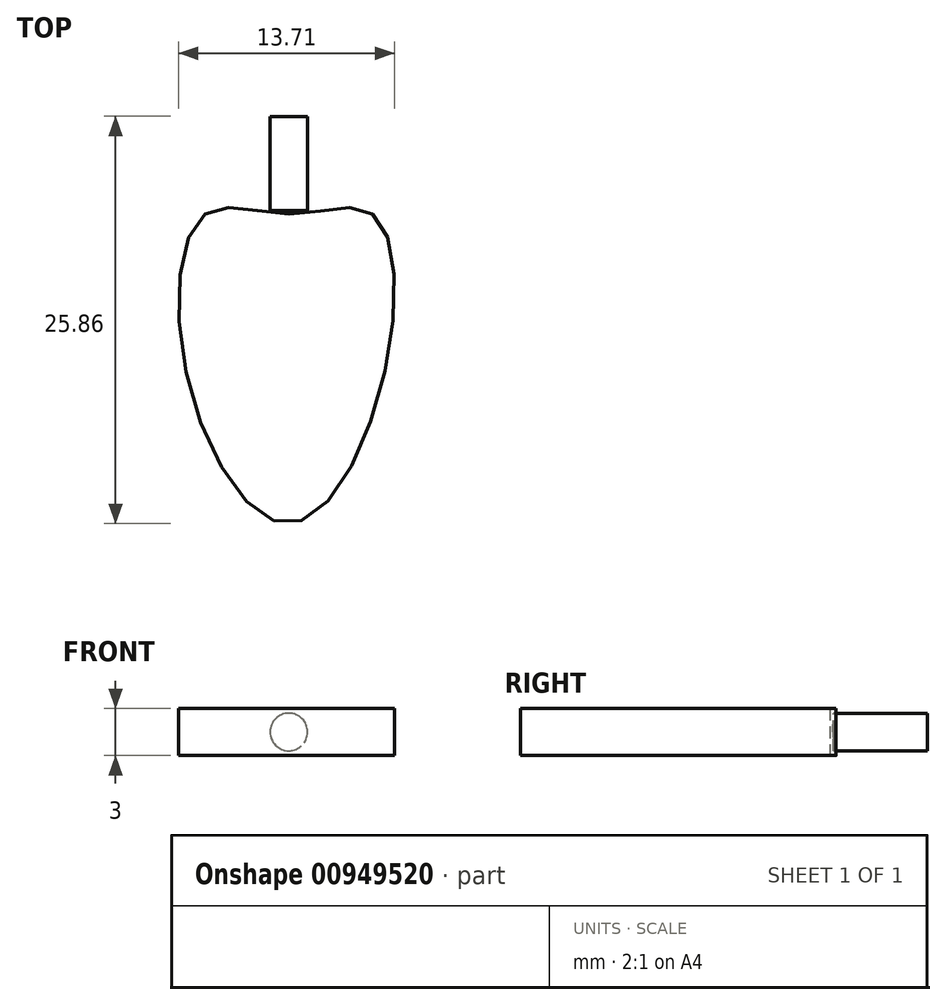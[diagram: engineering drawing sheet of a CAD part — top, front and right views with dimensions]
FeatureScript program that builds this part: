
annotation { "Feature Type Name" : "Feature", "Feature Type Description" : "" }
export const myFeature = defineFeature(function(context is Context, id is Id, definition is map)
    precondition{}
    {
        {
            var Q0;
            Q0=qCreatedBy(makeId("Top.planeOp"),FACE);
            var sketch = newSketch(context, id + "F0", { "sketchPlane" : qUnion([Q0])});
            skFitSpline(sketch, "E0", {"points": [v(0, 8.61) * mm, v(-5.3, 8.61) * mm, v(-6.32, -2.36) * mm, v(0, -11.04) * mm, v(5.93, -2.1) * mm, v(5.3, 8.61) * mm, v(0, 8.61) * mm]});
            skSolve(sketch);
        }
        {
            var Q0;
            Q0=makeQuery(id+"F0.imprint","IMPRINT",FACE,{"disambiguationData":[TD([[makeQuery(id+"F0.imprint","IMPRINT",EDGE,{"derivedFrom":sQuery(id+"F0.wireOp",EDGE,"E0")}),1.0]])]});
            extrude(context, id + "F1", {"entities" : qUnion([Q0]), "endBound" : BoundingType.SYMMETRIC, "depth" : 3 * mm, "offsetDistance" : 25.4 * mm});
        }
        {
            var Q0;
            Q0=qCreatedBy(makeId("Top.planeOp"),FACE);
            var sketch = newSketch(context, id + "F2", { "sketchPlane" : qUnion([Q0])});
            skLineSegment(sketch, "E1", {"start": v(-1.2, 8.85) * mm, "end": v(-1.2, 14.82) * mm});
            skLineSegment(sketch, "E2", {"start": v(0, 8.8) * mm, "end": v(0, 14.82) * mm});
            skLineSegment(sketch, "E3", {"start": v(0, 14.82) * mm, "end": v(-1.2, 14.82) * mm});
            skLineSegment(sketch, "E4", {"start": v(-1.2, 8.85) * mm, "end": v(0, 8.8) * mm});
            skSolve(sketch);
        }
        {
            var Q0;
            Q0=makeQuery(id+"F2.imprint","IMPRINT",FACE,{"disambiguationData":[TD([[makeQuery(id+"F2.imprint","IMPRINT",EDGE,{"derivedFrom":sQuery(id+"F2.wireOp",EDGE,"E1")}),-1.0]])]});
            var Q1;
            Q1=sQuery(id+"F2.wireOp",EDGE,"E2");
            revolve(context, id + "F3", {"operationType" : NewBodyOperationType.ADD, "surfaceOperationType" : NewSurfaceOperationType.NEW, "entities" : qUnion([Q0]), "axis" : qUnion([Q1]), "revolveType" : RevolveType.FULL});
        }
    });
